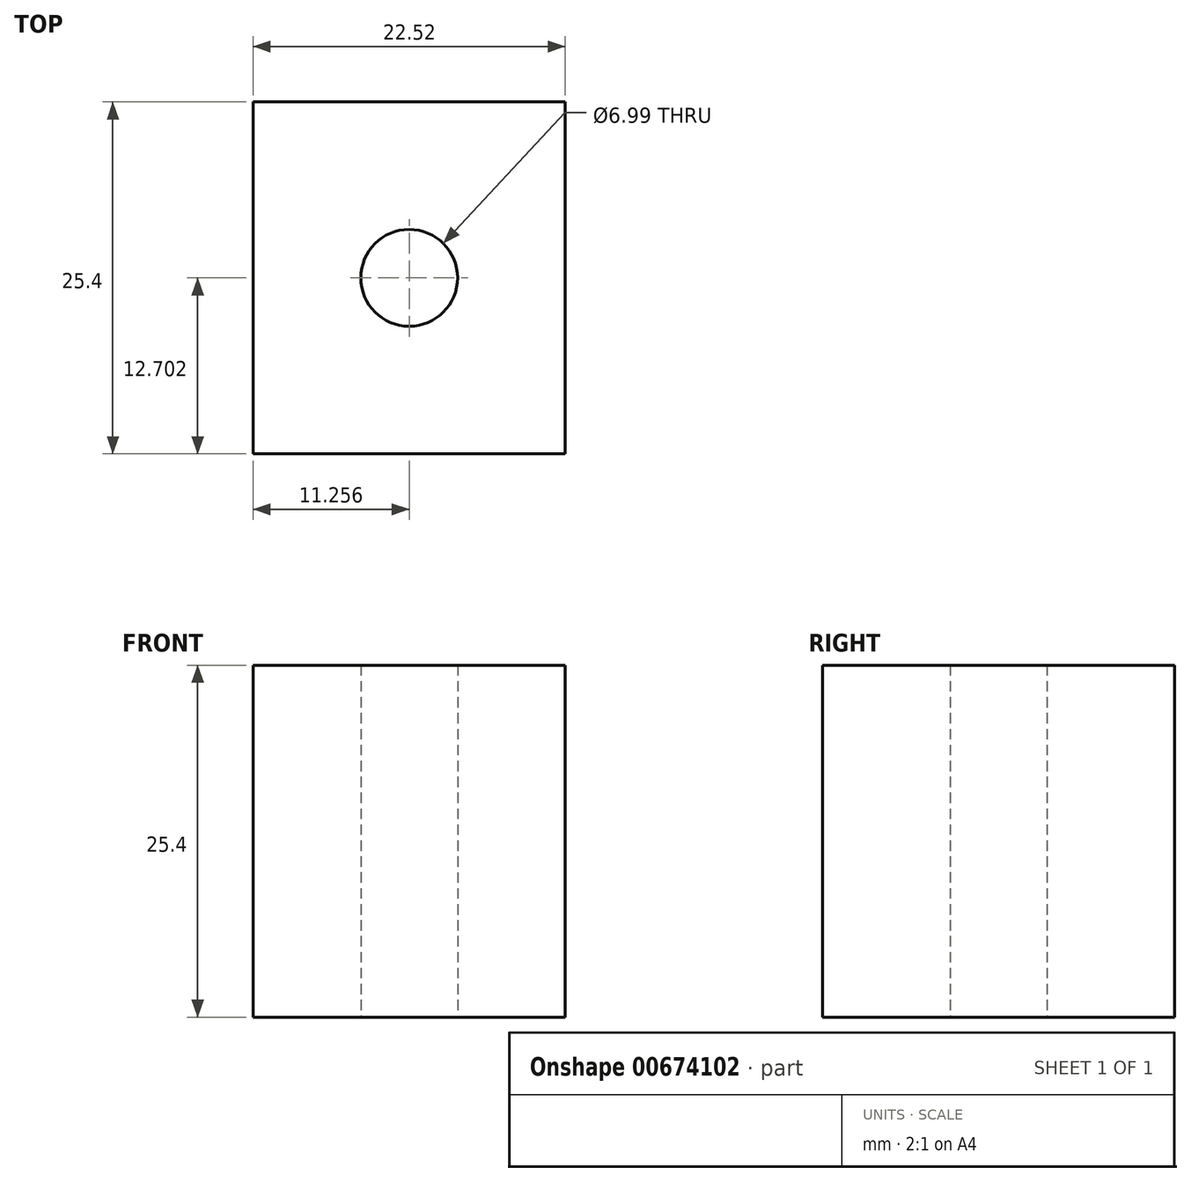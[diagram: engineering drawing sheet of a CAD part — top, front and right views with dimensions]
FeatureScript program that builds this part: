
annotation { "Feature Type Name" : "Feature", "Feature Type Description" : "" }
export const myFeature = defineFeature(function(context is Context, id is Id, definition is map)
    precondition{}
    {
        {
            var Q0;
            Q0=qCreatedBy(makeId("Top.planeOp"),FACE);
            var sketch = newSketch(context, id + "F0", { "sketchPlane" : qUnion([Q0])});
            skLineSegment(sketch, "E0.bottom", {"start": v(-71.81, 26.44) * mm, "end": v(-94.33, 26.44) * mm});
            skLineSegment(sketch, "E0.top", {"start": v(-71.81, 51.84) * mm, "end": v(-94.33, 51.84) * mm});
            skLineSegment(sketch, "E0.left", {"start": v(-71.81, 26.44) * mm, "end": v(-71.81, 51.84) * mm});
            skLineSegment(sketch, "E0.right", {"start": v(-94.33, 26.44) * mm, "end": v(-94.33, 51.84) * mm});
            skPoint(sketch, "E0.middle", {"position": v(-83.07, 39.14) * mm});
            skCircle(sketch, "E1", {"center": v(-83.07, 39.14) * mm, "radius": 3.5 * mm});
            skSolve(sketch);
        }
        {
            var Q0;
            Q0=makeQuery(id+"F0.imprint","IMPRINT",FACE,{"disambiguationData":[TD([[makeQuery(id+"F0.imprint","IMPRINT",EDGE,{"derivedFrom":sQuery(id+"F0.wireOp",EDGE,"E0.bottom")}),-1.0]])]});
            extrude(context, id + "F1", {"entities" : qUnion([Q0]), "depth" : 25.4 * mm, "offsetDistance" : 25.4 * mm});
        }
    });
